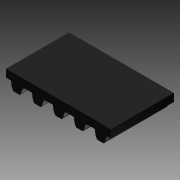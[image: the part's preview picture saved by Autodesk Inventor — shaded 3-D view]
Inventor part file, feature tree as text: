
AUTODESK INVENTOR PART (.ipt)
format: ipt  version: 2011 (Build 150239000, 239)  size: 138,752 bytes
history: native  units: in
note: dims shown in document units (in); Inventor stores cm internally (conversion verified against a paired STEP export)
features: extrude x1, sketch x1
ambient origin geometry x8: Origin, YZ Plane, XZ Plane, XY Plane, X Axis, Y Axis, Z Axis, Center Point
bodies: Solid1 (feature_tree)
feature tree (2):
  extrude  "Extrusion1"  Depth=0.1969in
  sketch  "Sketch1"  dims[d0=0.5906in d1=0.0in d2=0.1969in d3=0.15in d4=0.076in]
